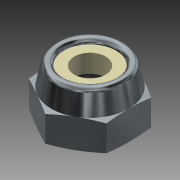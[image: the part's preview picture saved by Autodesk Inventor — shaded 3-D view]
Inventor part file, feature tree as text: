
AUTODESK INVENTOR PART (.ipt)
format: ipt  version: 2018 (Build 220112000, 112)  size: 224,768 bytes
history: native  units: mm (DEFAULTED — no unit token found)
features: sketch x5, extrude x2, revolve x2, other x1, plane x1, thread x1
ambient origin geometry x8: Origin, YZ Plane, XZ Plane, XY Plane, X Axis, Y Axis, Z Axis, Center Point
bodies: Solid1 (feature_tree)
feature tree (12):
  other  "Hexagon_flats_join1"
  extrude  "Extrusion1"  Depth=25.4mm TaperAngle=0.0deg
  revolve  "Revolution1"  Angle=90.0deg
  plane  "Work Plane1"
  extrude  "Extrusion2"  Depth=1.566333mm
  revolve  "Revolution2"  Angle=15.0deg
  thread  "Thread1"  [1 undecoded]
  sketch  "Sketch1"  dims[d0=9.525mm d3=25.4mm d4=0.0mm]
  sketch  "Sketch2"  dims[d5=13.788101mm d7=90.0deg]
  sketch  "Sketch3"  dims[d9=25.4mm d10=0.0mm d11=1.566333mm]
  sketch  "Sketch4"  dims[d12=15.0deg d13=15.0deg d14=9.525mm]
  sketch  "Sketch5"  dims[d15=90.0deg d16=25.4mm d17=0.0mm]
note: 1 required parameter value undecoded (feature->parameter linkage not recoverable at this tier; creation-order binding heuristic only, values carry confidence <= 0.55)
